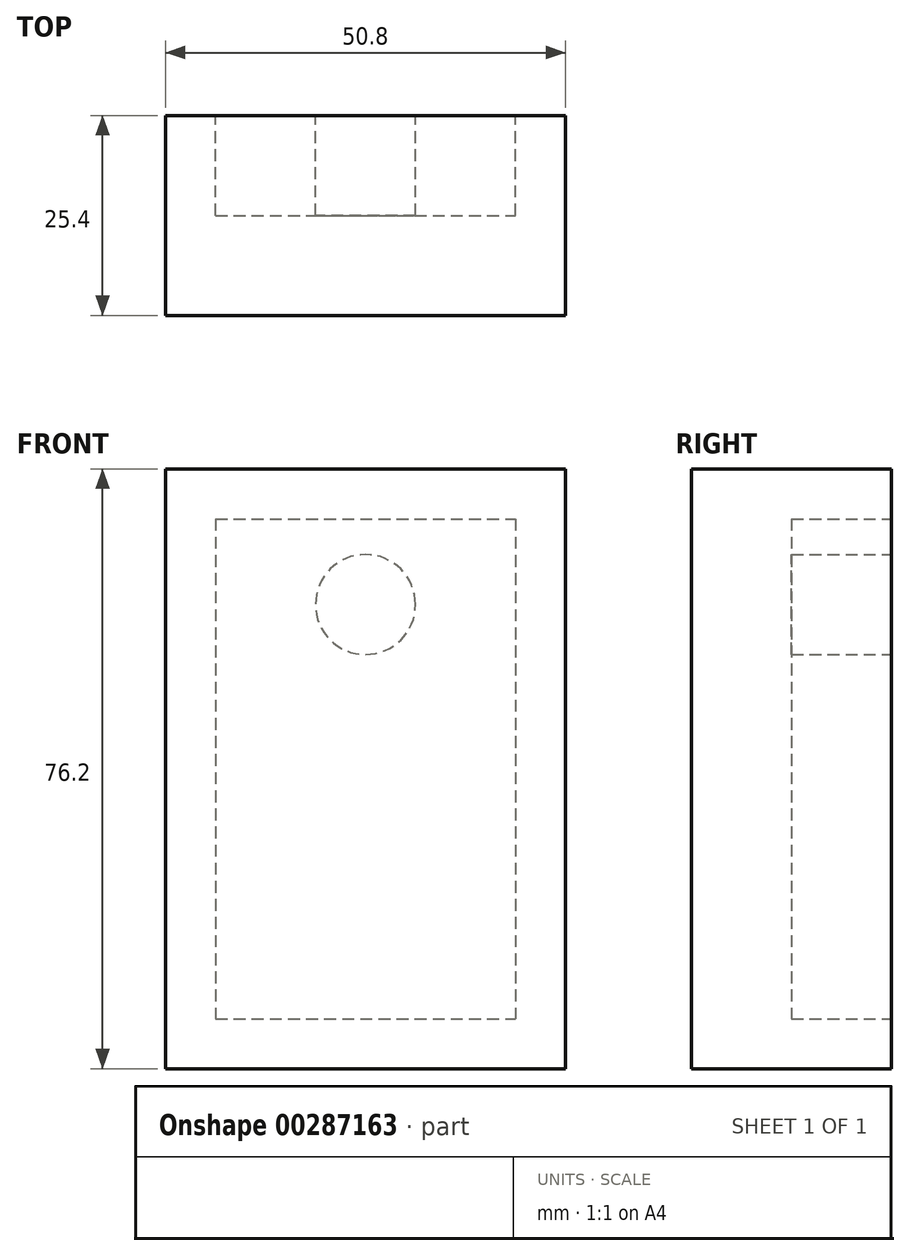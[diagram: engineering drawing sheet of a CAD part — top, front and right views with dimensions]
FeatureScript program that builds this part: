
annotation { "Feature Type Name" : "Feature", "Feature Type Description" : "" }
export const myFeature = defineFeature(function(context is Context, id is Id, definition is map)
    precondition{}
    {
        {
            var Q0;
            Q0=qCreatedBy(makeId("Front.planeOp"),FACE);
            var sketch = newSketch(context, id + "F0", { "sketchPlane" : qUnion([Q0])});
            skLineSegment(sketch, "E0.bottom", {"start": v(0, 0) * mm, "end": v(-50.8, 0) * mm});
            skLineSegment(sketch, "E0.top", {"start": v(0, 76.2) * mm, "end": v(-50.8, 76.2) * mm});
            skLineSegment(sketch, "E0.left", {"start": v(0, 0) * mm, "end": v(0, 76.2) * mm});
            skLineSegment(sketch, "E0.right", {"start": v(-50.8, 0) * mm, "end": v(-50.8, 76.2) * mm});
            skSolve(sketch);
        }
        {
            var Q0;
            Q0=makeQuery(id+"F0.imprint","IMPRINT",FACE,{"disambiguationData":[TD([[makeQuery(id+"F0.imprint","IMPRINT",EDGE,{"derivedFrom":sQuery(id+"F0.wireOp",EDGE,"E0.bottom")}),-1.0]])]});
            extrude(context, id + "F1", {"entities" : qUnion([Q0]), "depth" : 25.4 * mm});
        }
        {
            var Q0;
            Q0=qCreatedBy(makeId("Front.planeOp"),FACE);
            var sketch = newSketch(context, id + "F2", { "sketchPlane" : qUnion([Q0])});
            skLineSegment(sketch, "E1.bottom", {"start": v(-44.45, 69.85) * mm, "end": v(-6.35, 69.85) * mm});
            skLineSegment(sketch, "E1.top", {"start": v(-44.45, 6.35) * mm, "end": v(-6.35, 6.35) * mm});
            skLineSegment(sketch, "E1.left", {"start": v(-44.45, 69.85) * mm, "end": v(-44.45, 6.35) * mm});
            skLineSegment(sketch, "E1.right", {"start": v(-6.35, 69.85) * mm, "end": v(-6.35, 6.35) * mm});
            skSolve(sketch);
        }
        {
            var Q0;
            Q0 = qSketchRegion(id + "F2", true);
            extrude(context, id + "F3", {"entities" : qUnion([Q0]), "operationType" : NewBodyOperationType.REMOVE, "depth" : 12.7 * mm});
        }
        {
            var Q0;
            Q0=qCreatedBy(makeId("Front.planeOp"),FACE);
            var sketch = newSketch(context, id + "F4", { "sketchPlane" : qUnion([Q0])});
            skCircle(sketch, "E2", {"center": v(-25.4, 58.96) * mm, "radius": 6.35 * mm});
            skSolve(sketch);
        }
        {
            var Q0;
            Q0 = qSketchRegion(id + "F4", true);
            extrude(context, id + "F5", {"entities" : qUnion([Q0]), "operationType" : NewBodyOperationType.ADD, "depth" : 25.4 * mm});
        }
    });
